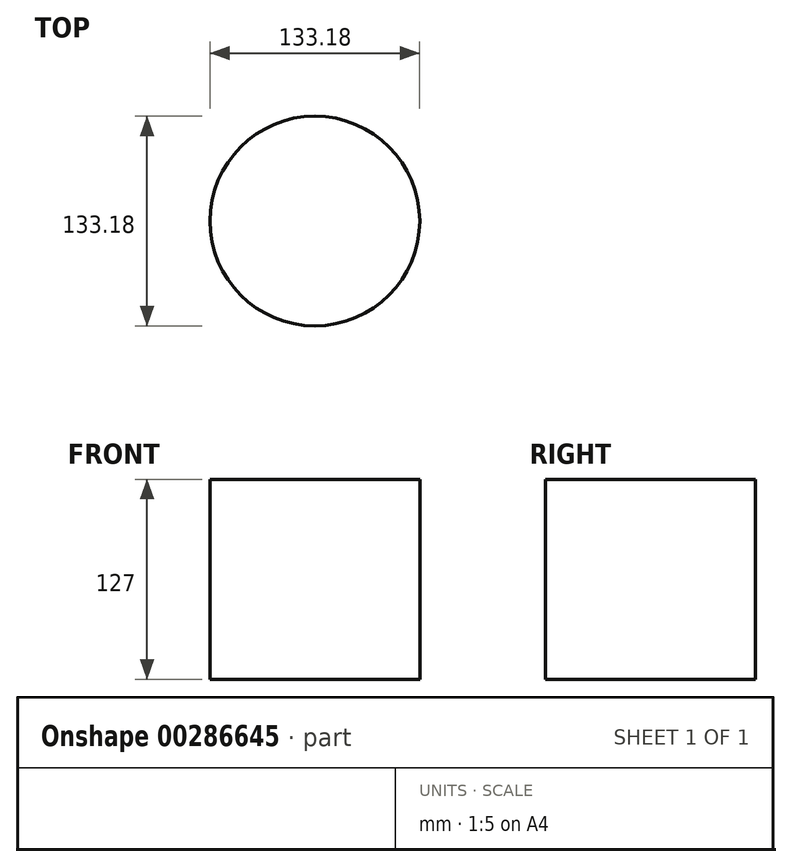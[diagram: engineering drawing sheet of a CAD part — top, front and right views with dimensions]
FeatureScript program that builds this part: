
annotation { "Feature Type Name" : "Feature", "Feature Type Description" : "" }
export const myFeature = defineFeature(function(context is Context, id is Id, definition is map)
    precondition{}
    {
        {
            var Q0;
            Q0=qCreatedBy(makeId("Top.planeOp"),FACE);
            var sketch = newSketch(context, id + "F0", { "sketchPlane" : qUnion([Q0])});
            skCircle(sketch, "E0", {"center": v(0, 0) * mm, "radius": 66.6 * mm});
            skSolve(sketch);
        }
        {
            var Q0;
            Q0 = qSketchRegion(id + "F0", true);
            extrude(context, id + "F1", {"entities" : qUnion([Q0]), "depth" : 127 * mm});
        }
    });
